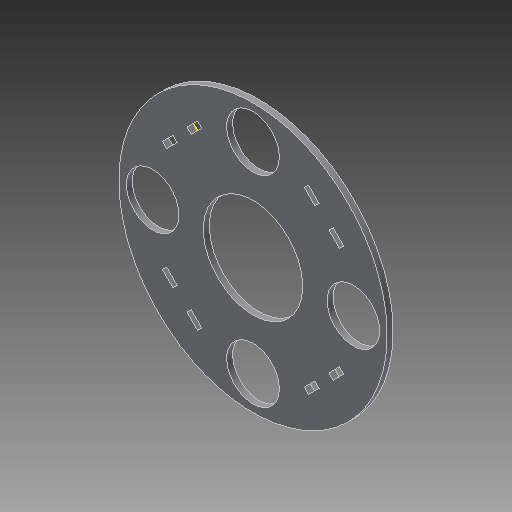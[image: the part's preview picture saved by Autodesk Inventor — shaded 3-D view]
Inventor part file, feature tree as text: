
AUTODESK INVENTOR PART (.ipt)
format: ipt  version: 2021.3 (Build 253353000, 353)  size: 161,792 bytes
history: native  units: mm
features: other x7, reference x6, extrude x1, sketch x1
ambient origin geometry x8: Origin, YZ Plane, XZ Plane, XY Plane, X Axis, Y Axis, Z Axis, Center Point
bodies: Body1 (feature_tree)
feature tree (15):
  other  "Твердое тело1"
  other  "РабПлоскость1"
  extrude  "Выдавливание1"  Depth=6.0mm TaperAngle=0.0deg
  sketch  "Эскиз1"
  reference  "Ссылка1"
  reference  "Ссылка2"
  reference  "Ссылка3"
  reference  "Ссылка4"
  reference  "Ссылка5"
  reference  "Ссылка6"
  parser-record x1  (decoder bookkeeping rows leaked as tree rows — omitted from the tree; the rows remain in map.json)
  other  "Поворотный_модуль_В5.iam"
  other  "Диск_базирующий_В5:1"
  other  "Диск_опорный_В5:1"
  other  "Стойка_В5:1"
note: 1 file-system path scrubbed to <path> (originals preserved in map.json)
